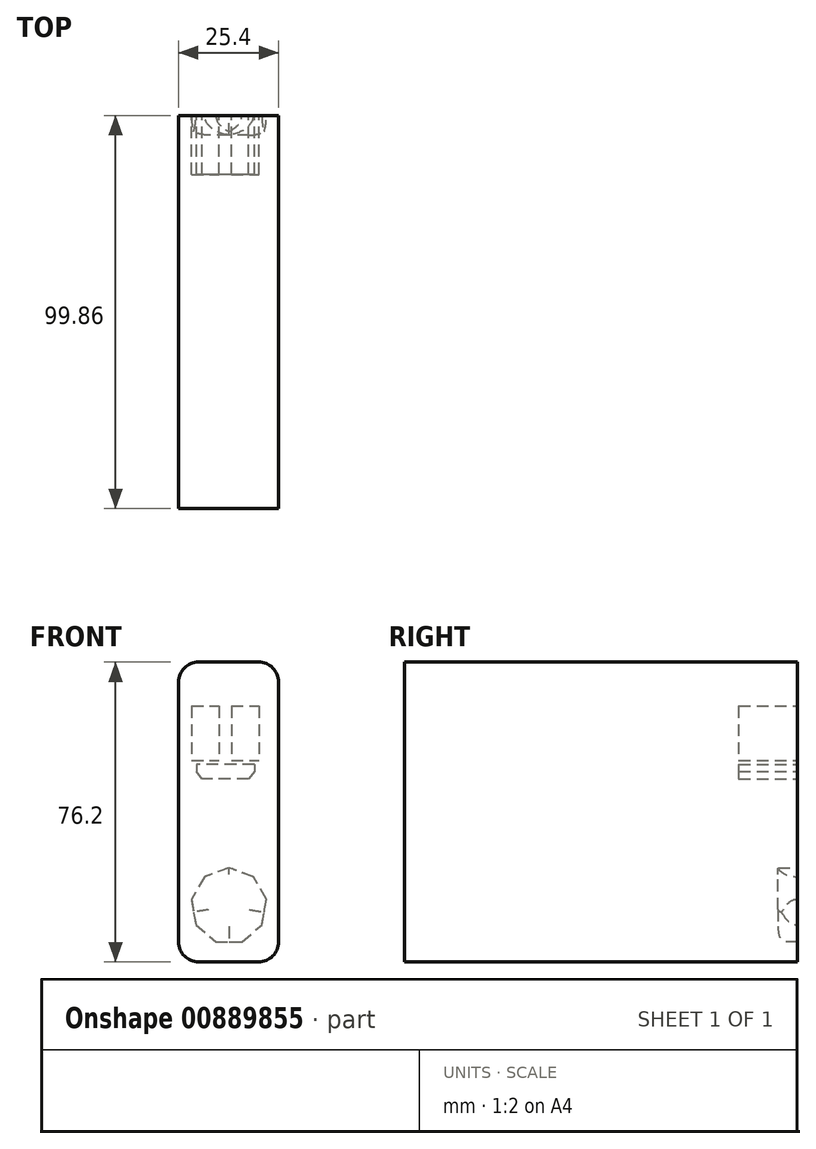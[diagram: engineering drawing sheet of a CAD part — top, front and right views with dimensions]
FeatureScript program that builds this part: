
annotation { "Feature Type Name" : "Feature", "Feature Type Description" : "" }
export const myFeature = defineFeature(function(context is Context, id is Id, definition is map)
    precondition{}
    {
        {
            var Q0;
            Q0=qCreatedBy(makeId("Right.planeOp"),FACE);
            var sketch = newSketch(context, id + "F0", { "sketchPlane" : qUnion([Q0])});
            skLineSegment(sketch, "E0.bottom", {"start": v(49.93, -38.1) * mm, "end": v(-49.93, -38.1) * mm});
            skLineSegment(sketch, "E0.top", {"start": v(49.93, 38.1) * mm, "end": v(-49.93, 38.1) * mm});
            skLineSegment(sketch, "E0.left", {"start": v(49.93, -38.1) * mm, "end": v(49.93, 38.1) * mm});
            skLineSegment(sketch, "E0.right", {"start": v(-49.93, -38.1) * mm, "end": v(-49.93, 38.1) * mm});
            skPoint(sketch, "E0.middle", {"position": v(0, 0) * mm});
            skSolve(sketch);
        }
        {
            var Q0;
            Q0 = qSketchRegion(id + "F0", true);
            extrude(context, id + "F1", {"entities" : qUnion([Q0]), "depth" : 25.4 * mm, "offsetDistance" : 25.4 * mm});
        }
        {
            var Q0;
            Q0=makeQuery(id+"F1.opExtrude","CAP_EDGE",EDGE,{"disambiguationData":[OSD([sQuery(id+"F0.wireOp",EDGE,"E0.top")])],"isStart":false});
            fillet(context, id + "F2", {"entities" : qUnion([Q0]), "radius" : 5.08 * mm, "tangentPropagation" : true, "allowEdgeOverflow" : false});
        }
        {
            var Q0;
            Q0=makeQuery(id+"F1.opExtrude","CAP_EDGE",EDGE,{"disambiguationData":[OSD([sQuery(id+"F0.wireOp",EDGE,"E0.top")])],"isStart":true});
            fillet(context, id + "F3", {"entities" : qUnion([Q0]), "radius" : 5.08 * mm, "tangentPropagation" : true, "allowEdgeOverflow" : false});
        }
        {
            var Q0;
            Q0=makeQuery(id+"F1.opExtrude","CAP_EDGE",EDGE,{"disambiguationData":[OSD([sQuery(id+"F0.wireOp",EDGE,"E0.bottom")])],"isStart":false});
            fillet(context, id + "F4", {"entities" : qUnion([Q0]), "radius" : 5.08 * mm, "tangentPropagation" : true, "allowEdgeOverflow" : false});
        }
        {
            var Q0;
            Q0=makeQuery(id+"F1.opExtrude","CAP_EDGE",EDGE,{"disambiguationData":[OSD([sQuery(id+"F0.wireOp",EDGE,"E0.bottom")])],"isStart":true});
            fillet(context, id + "F5", {"entities" : qUnion([Q0]), "radius" : 5.08 * mm, "tangentPropagation" : true, "allowEdgeOverflow" : false});
        }
        {
            var Q0;
            Q0=makeQuery(id+"F1.opExtrude","SWEPT_FACE",FACE,{"disambiguationData":[OSD([sQuery(id+"F0.wireOp",EDGE,"E0.left")])]});
            var sketch = newSketch(context, id + "F6", { "sketchPlane" : qUnion([Q0])});
            skLineSegment(sketch, "E1.bottom", {"start": v(-3.33, 26.9) * mm, "end": v(-10.33, 26.9) * mm});
            skLineSegment(sketch, "E1.top", {"start": v(-3.33, 13.1) * mm, "end": v(-10.33, 13.1) * mm});
            skLineSegment(sketch, "E1.left", {"start": v(-3.33, 26.9) * mm, "end": v(-3.33, 13.1) * mm});
            skLineSegment(sketch, "E1.right", {"start": v(-10.33, 26.9) * mm, "end": v(-10.33, 13.1) * mm});
            skLineSegment(sketch, "E2.bottom", {"start": v(-13.4, 26.9) * mm, "end": v(-20.4, 26.9) * mm});
            skLineSegment(sketch, "E2.top", {"start": v(-13.4, 13.1) * mm, "end": v(-20.4, 13.1) * mm});
            skLineSegment(sketch, "E2.left", {"start": v(-13.4, 26.9) * mm, "end": v(-13.4, 13.1) * mm});
            skLineSegment(sketch, "E2.right", {"start": v(-20.4, 26.9) * mm, "end": v(-20.4, 13.1) * mm});
            skSolve(sketch);
        }
        {
            var Q0;
            Q0 = qSketchRegion(id + "F6", true);
            extrude(context, id + "F7", {"entities" : qUnion([Q0]), "operationType" : NewBodyOperationType.REMOVE, "oppositeDirection" : true, "depth" : 15 * mm, "offsetDistance" : 25.4 * mm});
        }
        {
            var Q0;
            Q0=makeQuery(id+"F1.opExtrude","SWEPT_FACE",FACE,{"disambiguationData":[OSD([sQuery(id+"F0.wireOp",EDGE,"E0.left")])]});
            var sketch = newSketch(context, id + "F8", { "sketchPlane" : qUnion([Q0])});
            skLineSegment(sketch, "E3.bottom", {"start": v(-19.27, 12.08) * mm, "end": v(-4.54, 12.08) * mm});
            skLineSegment(sketch, "E3.top", {"start": v(-19.27, 10.29) * mm, "end": v(-4.54, 10.29) * mm});
            skLineSegment(sketch, "E3.left", {"start": v(-19.27, 12.08) * mm, "end": v(-19.27, 10.29) * mm});
            skLineSegment(sketch, "E3.right", {"start": v(-4.54, 12.08) * mm, "end": v(-4.54, 10.29) * mm});
            skLineSegment(sketch, "E4", {"start": v(-19.27, 10.29) * mm, "end": v(-17.8, 8.38) * mm});
            skLineSegment(sketch, "E5", {"start": v(-17.8, 8.38) * mm, "end": v(-5.94, 8.38) * mm});
            skLineSegment(sketch, "E6", {"start": v(-5.94, 8.38) * mm, "end": v(-4.54, 10.29) * mm});
            skSolve(sketch);
        }
        {
            var Q0;
            Q0 = qSketchRegion(id + "F8", true);
            extrude(context, id + "F9", {"entities" : qUnion([Q0]), "operationType" : NewBodyOperationType.REMOVE, "oppositeDirection" : true, "depth" : 15 * mm, "offsetDistance" : 25.4 * mm});
        }
        {
            var Q0;
            Q0=makeQuery(id+"F1.opExtrude","SWEPT_FACE",FACE,{"disambiguationData":[OSD([sQuery(id+"F0.wireOp",EDGE,"E0.left")])]});
            var sketch = newSketch(context, id + "F10", { "sketchPlane" : qUnion([Q0])});
            skCircle(sketch, "E7.cCircle", {"center": v(-12.77, -23.87) * mm, "radius": 9.1 * mm, "construction": true});
            skLineSegment(sketch, "E7.0", {"start": v(-9.46, -32.96) * mm, "end": v(-16.08, -32.96) * mm});
            skLineSegment(sketch, "E7.1", {"start": v(-16.08, -32.96) * mm, "end": v(-21.15, -28.7) * mm});
            skLineSegment(sketch, "E7.2", {"start": v(-21.15, -28.7) * mm, "end": v(-22.3, -22.19) * mm});
            skLineSegment(sketch, "E7.3", {"start": v(-22.3, -22.19) * mm, "end": v(-19, -16.46) * mm});
            skLineSegment(sketch, "E7.4", {"start": v(-19, -16.46) * mm, "end": v(-12.77, -14.2) * mm});
            skLineSegment(sketch, "E7.5", {"start": v(-12.77, -14.2) * mm, "end": v(-6.55, -16.46) * mm});
            skLineSegment(sketch, "E7.6", {"start": v(-6.55, -16.46) * mm, "end": v(-3.24, -22.19) * mm});
            skLineSegment(sketch, "E7.7", {"start": v(-3.24, -22.19) * mm, "end": v(-4.4, -28.7) * mm});
            skLineSegment(sketch, "E7.8", {"start": v(-4.4, -28.7) * mm, "end": v(-9.46, -32.96) * mm});
            skPoint(sketch, "E7.0.midPoint", {"position": v(-12.77, -32.96) * mm});
            skSolve(sketch);
        }
        {
            var Q0;
            Q0 = qSketchRegion(id + "F10", true);
            extrude(context, id + "F11", {"entities" : qUnion([Q0]), "operationType" : NewBodyOperationType.REMOVE, "oppositeDirection" : true, "depth" : 5 * mm, "offsetDistance" : 25.4 * mm});
        }
        {
            var Q0;
            Q0=makeQuery(id+"F11.boolean.opBoolean","COPY",EDGE,{"derivedFrom":makeQuery(id+"F11.opExtrude","CAP_EDGE",EDGE,{"disambiguationData":[OSD([sQuery(id+"F10.wireOp",EDGE,"E7.3")])],"isStart":false})});
            var Q1;
            Q1=makeQuery(id+"F11.boolean.opBoolean","COPY",EDGE,{"derivedFrom":makeQuery(id+"F11.opExtrude","CAP_EDGE",EDGE,{"disambiguationData":[OSD([sQuery(id+"F10.wireOp",EDGE,"E7.8")])],"isStart":false})});
            var Q2;
            Q2=makeQuery(id+"F11.boolean.opBoolean","COPY",EDGE,{"derivedFrom":makeQuery(id+"F11.opExtrude","CAP_EDGE",EDGE,{"disambiguationData":[OSD([sQuery(id+"F10.wireOp",EDGE,"E7.6")])],"isStart":false})});
            var Q3;
            Q3=makeQuery(id+"F11.boolean.opBoolean","COPY",EDGE,{"derivedFrom":makeQuery(id+"F11.opExtrude","CAP_EDGE",EDGE,{"disambiguationData":[OSD([sQuery(id+"F10.wireOp",EDGE,"E7.1")])],"isStart":false})});
            fillet(context, id + "F12", {"entities" : qUnion([Q0, Q1, Q2, Q3]), "radius" : 5.08 * mm, "tangentPropagation" : true, "allowEdgeOverflow" : false});
        }
    });
